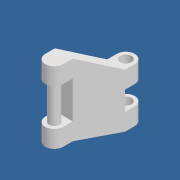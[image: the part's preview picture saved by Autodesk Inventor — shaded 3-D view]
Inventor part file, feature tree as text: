
AUTODESK INVENTOR PART (.ipt)
format: ipt  version: 2020 (Build 240168000, 168)  size: 153,600 bytes
history: native  units: mm
features: extrude x5, sketch x5, fillet x1
ambient origin geometry x8: Origin, YZ Plane, XZ Plane, XY Plane, X Axis, Y Axis, Z Axis, Center Point
bodies: Solid1 (feature_tree)
feature tree (11):
  extrude  "Extrusion1"  Depth=8.0mm TaperAngle=0.0deg
  extrude  "Extrusion6"  Depth=8.0mm
  extrude  "Extrusion7"  Depth=8.0mm
  extrude  "Extrusion8"  Depth=8.0mm
  extrude  "Extrusion9"  Depth=8.3mm TaperAngle=0.0deg
  fillet  "Fillet2"  Radius=8.0mm
  sketch  "Sketch2"  dims[d4=32.0mm d7=8.0mm d8=0.0mm]
  sketch  "Sketch7"  dims[d32=24.0mm d34=8.0mm]
  sketch  "Sketch8"  dims[d35=23.4mm d36=8.0mm]
  sketch  "Sketch9"  dims[d37=7.7mm d38=8.0mm]
  sketch  "Sketch10"  dims[d39=7.7mm d40=8.3mm d41=0.0mm d42=8.0mm d43=7.7mm d44=8.0mm d45=7.7mm d46=8.3mm d47=0.0mm d48=4.6mm d49=4.0mm d50=4.0mm d51=8.3mm d52=0.0mm d53=5.0mm d54=4.0mm d55=4.0mm d56=8.3mm d57=0.0mm d58=4.0mm]
